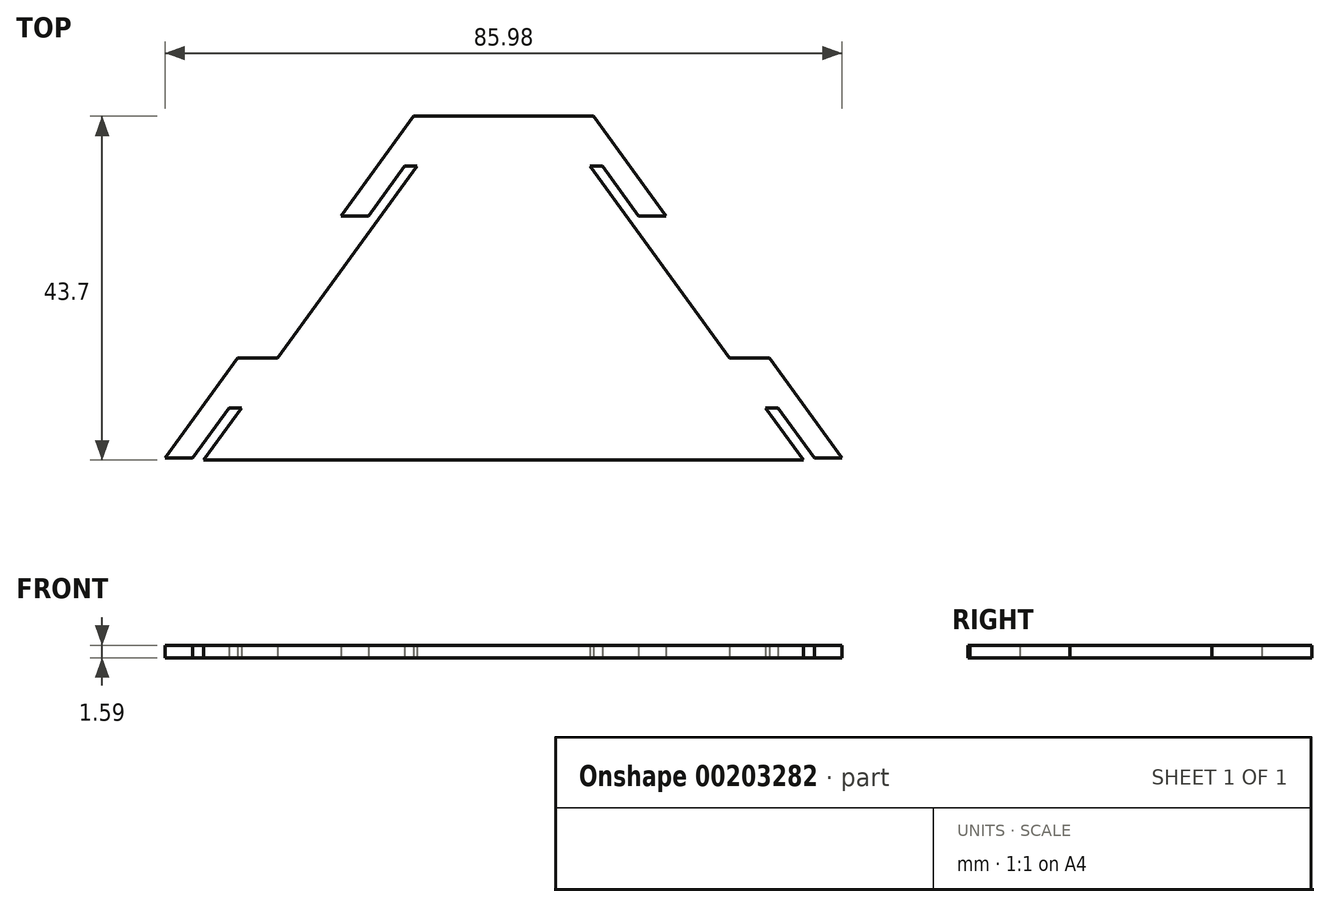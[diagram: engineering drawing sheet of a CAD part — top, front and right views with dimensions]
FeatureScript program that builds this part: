
annotation { "Feature Type Name" : "Feature", "Feature Type Description" : "" }
export const myFeature = defineFeature(function(context is Context, id is Id, definition is map)
    precondition{}
    {
        {
            var Q0;
            Q0=qCreatedBy(makeId("Top.planeOp"),FACE);
            var sketch = newSketch(context, id + "F0", { "sketchPlane" : qUnion([Q0])});
            skLineSegment(sketch, "E0", {"start": v(0, 0) * mm, "end": v(76.2, 0) * mm, "construction": true});
            skLineSegment(sketch, "E1", {"start": v(76.2, 0) * mm, "end": v(44.45, 43.7) * mm, "construction": true});
            skLineSegment(sketch, "E2", {"start": v(44.45, 43.7) * mm, "end": v(31.75, 43.7) * mm, "construction": true});
            skLineSegment(sketch, "E3", {"start": v(31.75, 43.7) * mm, "end": v(0, 0) * mm, "construction": true});
            skLineSegment(sketch, "E4", {"start": v(31.75, 43.7) * mm, "end": v(26.67, 43.7) * mm});
            skLineSegment(sketch, "E5", {"start": v(26.67, 43.7) * mm, "end": v(17.44, 31) * mm});
            skLineSegment(sketch, "E6", {"start": v(17.44, 31) * mm, "end": v(20.94, 31) * mm});
            skLineSegment(sketch, "E7", {"start": v(20.94, 31) * mm, "end": v(25.55, 37.35) * mm});
            skLineSegment(sketch, "E8", {"start": v(25.55, 37.35) * mm, "end": v(27.14, 37.35) * mm});
            skLineSegment(sketch, "E9", {"start": v(27.14, 37.35) * mm, "end": v(9.42, 12.97) * mm});
            skLineSegment(sketch, "E10", {"start": v(9.42, 12.97) * mm, "end": v(4.34, 12.97) * mm});
            skLineSegment(sketch, "E11", {"start": v(4.34, 12.97) * mm, "end": v(-4.89, 0.27) * mm});
            skLineSegment(sketch, "E12", {"start": v(-4.89, 0.27) * mm, "end": v(-1.4, 0.27) * mm});
            skLineSegment(sketch, "E13", {"start": v(-1.4, 0.27) * mm, "end": v(3.22, 6.62) * mm});
            skLineSegment(sketch, "E14", {"start": v(3.22, 6.62) * mm, "end": v(4.8, 6.62) * mm});
            skLineSegment(sketch, "E15", {"start": v(38.1, 43.7) * mm, "end": v(38.1, 0) * mm, "construction": true});
            skLineSegment(sketch, "E16", {"start": v(4.8, 6.62) * mm, "end": v(0, 0) * mm});
            skLineSegment(sketch, "E17", {"start": v(38.1, 0) * mm, "end": v(0, 0) * mm});
            skLineSegment(sketch, "E18", {"start": v(31.75, 43.7) * mm, "end": v(38.1, 43.7) * mm});
            skLineSegment(sketch, "E19.MirrorCS", {"start": v(58.76, 31) * mm, "end": v(55.26, 31) * mm});
            skLineSegment(sketch, "E20.MirrorCS", {"start": v(72.98, 6.62) * mm, "end": v(71.4, 6.62) * mm});
            skLineSegment(sketch, "E21.MirrorCS", {"start": v(81.09, 0.27) * mm, "end": v(77.6, 0.27) * mm});
            skLineSegment(sketch, "E22.MirrorCS", {"start": v(50.65, 37.35) * mm, "end": v(49.06, 37.35) * mm});
            skLineSegment(sketch, "E23.MirrorCS", {"start": v(71.4, 6.62) * mm, "end": v(76.2, 0) * mm});
            skLineSegment(sketch, "E24.MirrorCS", {"start": v(49.06, 37.35) * mm, "end": v(66.78, 12.97) * mm});
            skLineSegment(sketch, "E25.MirrorCS", {"start": v(44.45, 43.7) * mm, "end": v(49.53, 43.7) * mm});
            skLineSegment(sketch, "E26.MirrorCS", {"start": v(71.86, 12.97) * mm, "end": v(81.09, 0.27) * mm});
            skLineSegment(sketch, "E27.MirrorCS", {"start": v(38.1, 0) * mm, "end": v(76.2, 0) * mm});
            skLineSegment(sketch, "E28.MirrorCS", {"start": v(77.6, 0.27) * mm, "end": v(72.98, 6.62) * mm});
            skLineSegment(sketch, "E29.MirrorCS", {"start": v(44.45, 43.7) * mm, "end": v(38.1, 43.7) * mm});
            skLineSegment(sketch, "E30.MirrorCS", {"start": v(49.53, 43.7) * mm, "end": v(58.76, 31) * mm});
            skLineSegment(sketch, "E31.MirrorCS", {"start": v(66.78, 12.97) * mm, "end": v(71.86, 12.97) * mm});
            skLineSegment(sketch, "E32.MirrorCS", {"start": v(55.26, 31) * mm, "end": v(50.65, 37.35) * mm});
            skSolve(sketch);
        }
        {
            var Q0;
            Q0=makeQuery(id+"F0.imprint","IMPRINT",FACE,{"disambiguationData":[TD([[makeQuery(id+"F0.imprint","IMPRINT",EDGE,{"derivedFrom":sQuery(id+"F0.wireOp",EDGE,"E4")}),1.0]])]});
            extrude(context, id + "F1", {"entities" : qUnion([Q0]), "depth" : 1.59 * mm});
        }
    });
